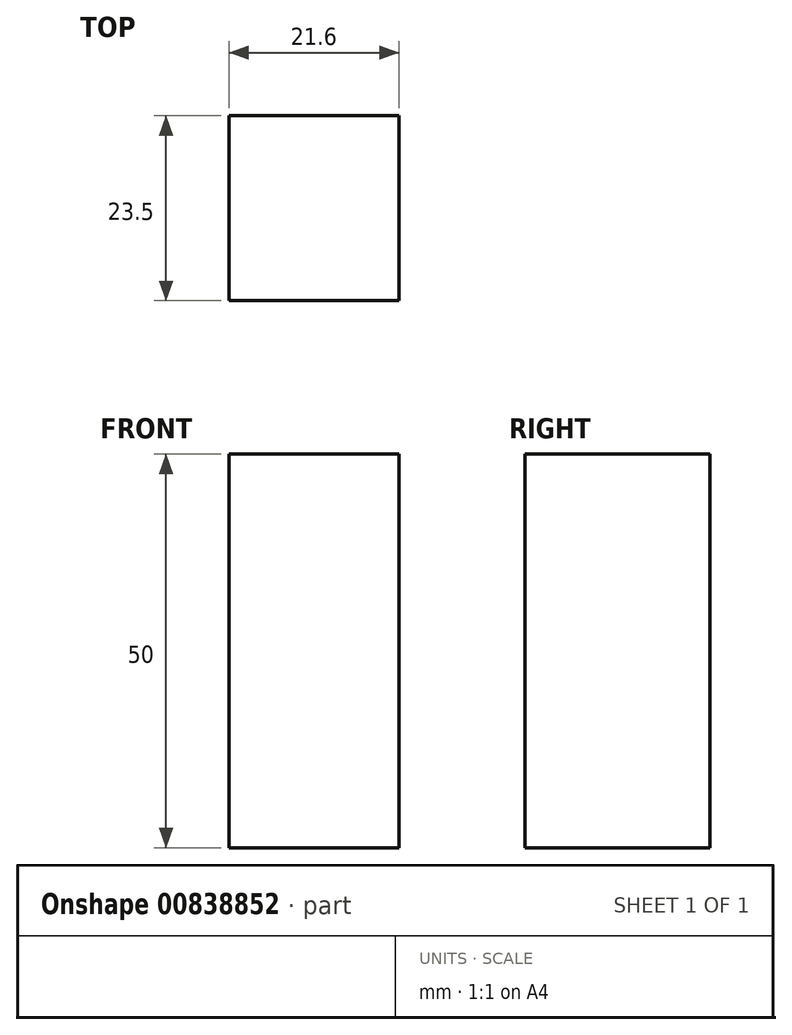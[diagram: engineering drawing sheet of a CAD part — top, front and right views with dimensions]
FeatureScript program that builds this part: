
annotation { "Feature Type Name" : "Feature", "Feature Type Description" : "" }
export const myFeature = defineFeature(function(context is Context, id is Id, definition is map)
    precondition{}
    {
        {
            var Q0;
            Q0=qCreatedBy(makeId("Top.planeOp"),FACE);
            var sketch = newSketch(context, id + "F0", { "sketchPlane" : qUnion([Q0])});
            skLineSegment(sketch, "E0.bottom", {"start": v(10.8, -11.75) * mm, "end": v(-10.8, -11.75) * mm});
            skLineSegment(sketch, "E0.top", {"start": v(10.8, 11.75) * mm, "end": v(-10.8, 11.75) * mm});
            skLineSegment(sketch, "E0.left", {"start": v(10.8, -11.75) * mm, "end": v(10.8, 11.75) * mm});
            skLineSegment(sketch, "E0.right", {"start": v(-10.8, -11.75) * mm, "end": v(-10.8, 11.75) * mm});
            skPoint(sketch, "E0.middle", {"position": v(0, 0) * mm});
            skSolve(sketch);
        }
        {
            var Q0;
            Q0 = qSketchRegion(id + "F0", true);
            extrude(context, id + "F1", {"entities" : qUnion([Q0]), "depth" : 50 * mm, "offsetDistance" : 25 * mm});
        }
    });
